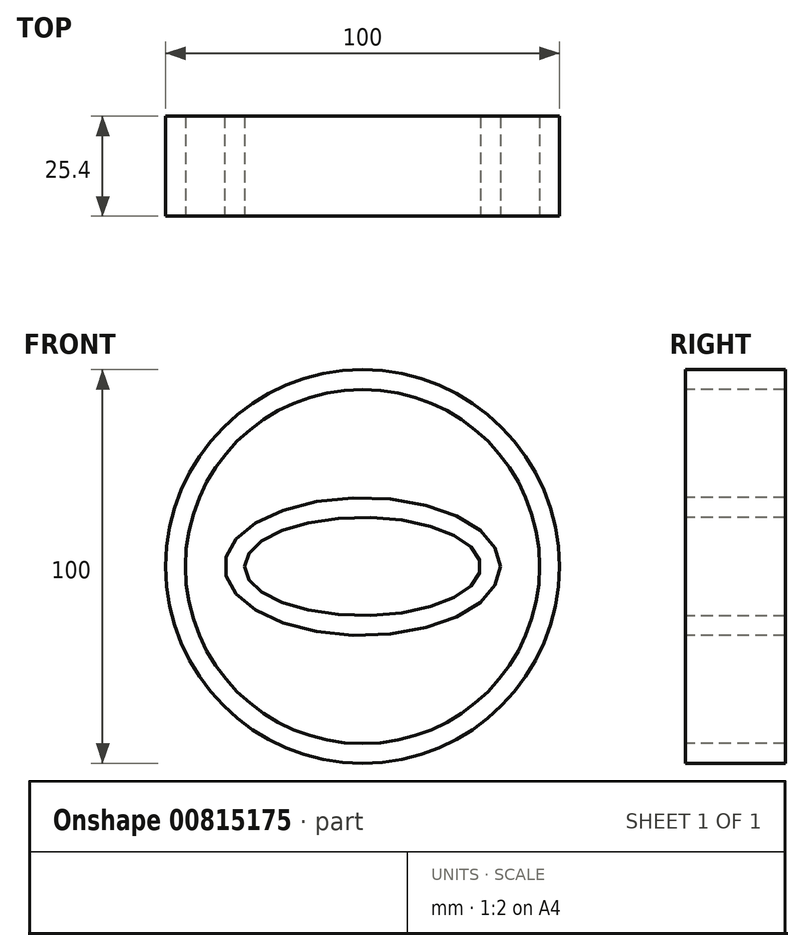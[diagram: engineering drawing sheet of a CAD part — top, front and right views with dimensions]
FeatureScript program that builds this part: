
annotation { "Feature Type Name" : "Feature", "Feature Type Description" : "" }
export const myFeature = defineFeature(function(context is Context, id is Id, definition is map)
    precondition{}
    {
        {
            var Q0;
            Q0=qCreatedBy(makeId("Front.planeOp"),FACE);
            var sketch = newSketch(context, id + "F0", { "sketchPlane" : qUnion([Q0])});
            skCircle(sketch, "E0", {"center": v(0, 0) * mm, "radius": 50 * mm});
            skSolve(sketch);
        }
        {
            var Q0;
            Q0=makeQuery(id+"F0.imprint","IMPRINT",FACE,{"disambiguationData":[TD([[makeQuery(id+"F0.imprint","IMPRINT",EDGE,{"derivedFrom":sQuery(id+"F0.wireOp",EDGE,"E0")}),1.0]])]});
            var sketch = newSketch(context, id + "F1", { "sketchPlane" : qUnion([Q0])});
            skEllipse(sketch, "E1", {"center": v(0, 0) * mm, "majorRadius": 30 * mm, "minorRadius": 12.5 * mm, "majorAxis": v(-1, 0)});
            skSolve(sketch);
        }
        {
            var Q0;
            Q0=qCreatedBy(makeId("Front.planeOp"),FACE);
            var sketch = newSketch(context, id + "F2", { "sketchPlane" : qUnion([Q0])});
            skCircle(sketch, "E2", {"center": v(0, 0) * mm, "radius": 45 * mm});
            skSolve(sketch);
        }
        {
            var Q0;
            Q0=qCreatedBy(makeId("Front.planeOp"),FACE);
            var sketch = newSketch(context, id + "F3", { "sketchPlane" : qUnion([Q0])});
            skEllipse(sketch, "E3", {"center": v(0, 0) * mm, "majorRadius": 35 * mm, "minorRadius": 17.5 * mm, "majorAxis": v(1, 0)});
            skSolve(sketch);
        }
        {
            var Q0;
            Q0=sQuery(id+"F1.wireOp",EDGE,"E1");
            var Q1;
            Q1=sQuery(id+"F3.wireOp",EDGE,"E3");
            var Q2;
            Q2=sQuery(id+"F2.wireOp",EDGE,"E2");
            var Q3;
            Q3=sQuery(id+"F0.wireOp",EDGE,"E0");
            extrude(context, id + "F4", {"bodyType" : ToolBodyType.SURFACE, "surfaceEntities" : qUnion([Q0, Q1, Q2, Q3]), "depth" : 25.4 * mm, "offsetDistance" : 25.4 * mm});
        }
    });
